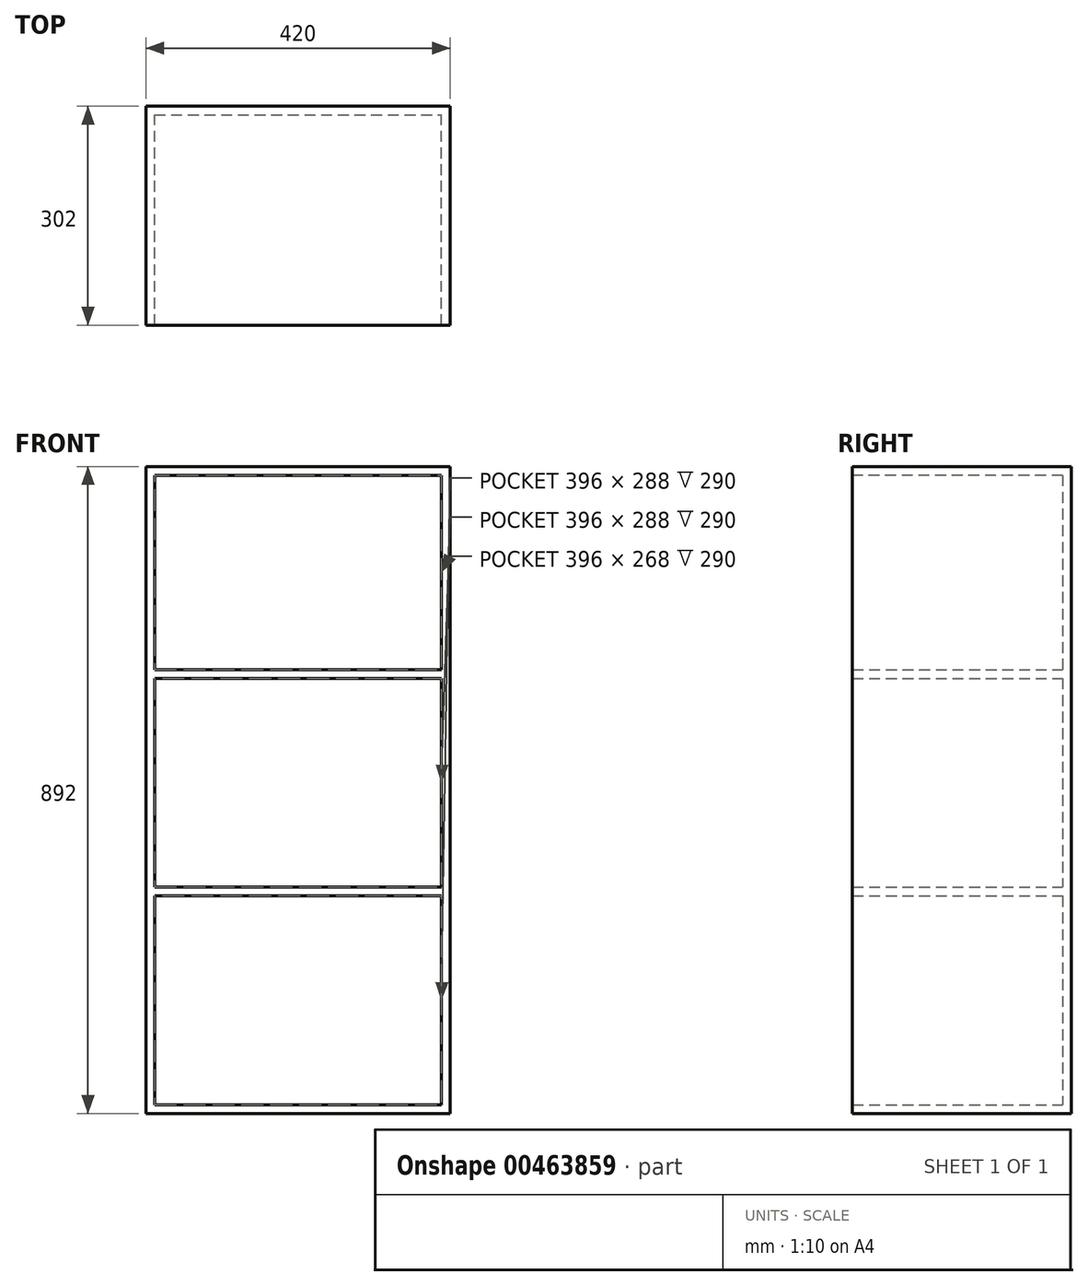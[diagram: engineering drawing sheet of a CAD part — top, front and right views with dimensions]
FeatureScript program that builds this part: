
annotation { "Feature Type Name" : "Feature", "Feature Type Description" : "" }
export const myFeature = defineFeature(function(context is Context, id is Id, definition is map)
    precondition{}
    {
        {
            var Q0;
            Q0=qCreatedBy(makeId("Top.planeOp"),FACE);
            var sketch = newSketch(context, id + "F0", { "sketchPlane" : qUnion([Q0])});
            skLineSegment(sketch, "E0.bottom", {"start": v(0, 0) * mm, "end": v(420, 0) * mm});
            skLineSegment(sketch, "E0.top", {"start": v(0, 290) * mm, "end": v(420, 290) * mm});
            skLineSegment(sketch, "E0.left", {"start": v(0, 0) * mm, "end": v(0, 290) * mm});
            skLineSegment(sketch, "E0.right", {"start": v(420, 0) * mm, "end": v(420, 290) * mm});
            skSolve(sketch);
        }
        {
            var Q0;
            Q0 = qSketchRegion(id + "F0", true);
            extrude(context, id + "F1", {"entities" : qUnion([Q0]), "depth" : 12 * mm});
        }
        {
            var Q0;
            Q0=makeQuery(id+"F1.opExtrude","CAP_FACE",FACE,{"disambiguationData":[OSD([sQuery(id+"F0.wireOp",EDGE,"E0.bottom"),sQuery(id+"F0.wireOp",EDGE,"E0.top"),sQuery(id+"F0.wireOp",EDGE,"E0.left"),sQuery(id+"F0.wireOp",EDGE,"E0.right")])],"isStart":false});
            var sketch = newSketch(context, id + "F2", { "sketchPlane" : qUnion([Q0])});
            skLineSegment(sketch, "E1.bottom", {"start": v(0, 0) * mm, "end": v(12, 0) * mm});
            skLineSegment(sketch, "E1.top", {"start": v(0, 290) * mm, "end": v(12, 290) * mm});
            skLineSegment(sketch, "E1.left", {"start": v(0, 0) * mm, "end": v(0, 290) * mm});
            skLineSegment(sketch, "E1.right", {"start": v(12, 0) * mm, "end": v(12, 290) * mm});
            skLineSegment(sketch, "E2.bottom", {"start": v(420, 0) * mm, "end": v(408, 0) * mm});
            skLineSegment(sketch, "E2.top", {"start": v(420, 290) * mm, "end": v(408, 290) * mm});
            skLineSegment(sketch, "E2.left", {"start": v(420, 0) * mm, "end": v(420, 290) * mm});
            skLineSegment(sketch, "E2.right", {"start": v(408, 0) * mm, "end": v(408, 290) * mm});
            skSolve(sketch);
        }
        {
            var Q0;
            Q0 = qSketchRegion(id + "F2", true);
            extrude(context, id + "F3", {"entities" : qUnion([Q0]), "operationType" : NewBodyOperationType.ADD, "depth" : 880 * mm});
        }
        {
            var Q0;
            Q0=makeQuery(id+"F3.boolean.opBoolean","MERGE",FACE,{"derivedFrom":[makeQuery(id+"F1.opExtrude","SWEPT_FACE",FACE,{"disambiguationData":[OSD([sQuery(id+"F0.wireOp",EDGE,"E0.right")])]}),makeQuery(id+"F3.opExtrude","SWEPT_FACE",FACE,{"disambiguationData":[OSD([sQuery(id+"F2.wireOp",EDGE,"E2.left")])]})]});
            var sketch = newSketch(context, id + "F4", { "sketchPlane" : qUnion([Q0])});
            skPoint(sketch, "E3", {"position": v(0, 300) * mm});
            skPoint(sketch, "E4", {"position": v(0, 600) * mm});
            skLineSegment(sketch, "E5", {"start": v(0, 600) * mm, "end": v(290, 600) * mm});
            skLineSegment(sketch, "E6", {"start": v(0, 300) * mm, "end": v(290, 300) * mm});
            skSolve(sketch);
        }
        {
            var Q0;
            Q0=qCreatedBy(makeId("Top.planeOp"),FACE);
            cPlane(context, id + "F5", {"entities" : qUnion([Q0]), "cplaneType" : CPlaneType.OFFSET, "offset" : 300 * mm, "width" : 152.4 * mm, "height" : 152.4 * mm});
        }
        {
            var Q0;
            Q0=qCreatedBy(makeId("Top.planeOp"),FACE);
            cPlane(context, id + "F6", {"entities" : qUnion([Q0]), "cplaneType" : CPlaneType.OFFSET, "offset" : 600 * mm, "width" : 152.4 * mm, "height" : 152.4 * mm});
        }
        {
            var Q0;
            Q0=qCreatedBy(id+"F5.planeOp",FACE);
            var sketch = newSketch(context, id + "F7", { "sketchPlane" : qUnion([Q0])});
            skLineSegment(sketch, "E7.bottom", {"start": v(0, 0) * mm, "end": v(420, 0) * mm});
            skLineSegment(sketch, "E7.top", {"start": v(0, 290) * mm, "end": v(420, 290) * mm});
            skLineSegment(sketch, "E7.left", {"start": v(0, 0) * mm, "end": v(0, 290) * mm});
            skLineSegment(sketch, "E7.right", {"start": v(420, 0) * mm, "end": v(420, 290) * mm});
            skSolve(sketch);
        }
        {
            var Q0;
            Q0 = qSketchRegion(id + "F7", true);
            extrude(context, id + "F8", {"entities" : qUnion([Q0]), "operationType" : NewBodyOperationType.ADD, "depth" : 12 * mm});
        }
        {
            var Q0;
            Q0=qCreatedBy(id+"F6.planeOp",FACE);
            var sketch = newSketch(context, id + "F9", { "sketchPlane" : qUnion([Q0])});
            skLineSegment(sketch, "E8.bottom", {"start": v(0, 0) * mm, "end": v(420, 0) * mm});
            skLineSegment(sketch, "E8.top", {"start": v(0, 290) * mm, "end": v(420, 290) * mm});
            skLineSegment(sketch, "E8.left", {"start": v(0, 0) * mm, "end": v(0, 290) * mm});
            skLineSegment(sketch, "E8.right", {"start": v(420, 0) * mm, "end": v(420, 290) * mm});
            skSolve(sketch);
        }
        {
            var Q0;
            Q0 = qSketchRegion(id + "F9", true);
            extrude(context, id + "F10", {"entities" : qUnion([Q0]), "operationType" : NewBodyOperationType.ADD, "depth" : 12 * mm});
        }
        {
            var Q0;
            Q0=makeQuery(id+"F3.opExtrude","CAP_EDGE",EDGE,{"disambiguationData":[OSD([sQuery(id+"F2.wireOp",EDGE,"E1.right")])],"isStart":false});
            cPoint(context, id + "F11", {"entities" : qUnion([Q0]), "parameter" : 0.5});
        }
        {
            var Q0;
            Q0=makeQuery(id+"F3.opExtrude","CAP_VERTEX",VERTEX,{"disambiguationData":[OSD([sQuery(id+"F2.wireOp",EDGE,"E1.bottom"),sQuery(id+"F2.wireOp",EDGE,"E1.left")])],"isStart":false});
            var Q1;
            Q1=makeQuery(id+"F3.opExtrude","CAP_VERTEX",VERTEX,{"disambiguationData":[OSD([sQuery(id+"F0.wireOp",EDGE,"E0.bottom"),sQuery(id+"F2.wireOp",EDGE,"E1.bottom"),sQuery(id+"F2.wireOp",EDGE,"E1.right")])],"isStart":false});
            var Q2;
            Q2 = qCreatedBy(id + "F11" ,VERTEX);
            cPlane(context, id + "F12", {"entities" : qUnion([Q0, Q1, Q2]), "cplaneType" : CPlaneType.THREE_POINT, "offset" : 25.4 * mm, "width" : 152.4 * mm, "height" : 152.4 * mm});
        }
        {
            var Q0;
            Q0=qCreatedBy(id+"F12.planeOp",FACE);
            var sketch = newSketch(context, id + "F13", { "sketchPlane" : qUnion([Q0])});
            skLineSegment(sketch, "E9.bottom", {"start": v(0, 0) * mm, "end": v(420, 0) * mm});
            skLineSegment(sketch, "E9.top", {"start": v(0, -290) * mm, "end": v(420, -290) * mm});
            skLineSegment(sketch, "E9.left", {"start": v(0, 0) * mm, "end": v(0, -290) * mm});
            skLineSegment(sketch, "E9.right", {"start": v(420, 0) * mm, "end": v(420, -290) * mm});
            skSolve(sketch);
        }
        {
            var Q0;
            Q0 = qSketchRegion(id + "F13", true);
            extrude(context, id + "F14", {"entities" : qUnion([Q0]), "operationType" : NewBodyOperationType.ADD, "depth" : 12 * mm});
        }
        {
            var Q0;
            Q0=makeQuery(id+"F14.boolean.opBoolean","MERGE",FACE,{"derivedFrom":[makeQuery(id+"F10.boolean.opBoolean","MERGE",FACE,{"derivedFrom":[makeQuery(id+"F8.boolean.opBoolean","MERGE",FACE,{"derivedFrom":[makeQuery(id+"F3.boolean.opBoolean","MERGE",FACE,{"derivedFrom":[makeQuery(id+"F1.opExtrude","SWEPT_FACE",FACE,{"disambiguationData":[OSD([sQuery(id+"F0.wireOp",EDGE,"E0.top")])]}),makeQuery(id+"F3.opExtrude","SWEPT_FACE",FACE,{"disambiguationData":[OSD([sQuery(id+"F2.wireOp",EDGE,"E1.top")])]}),makeQuery(id+"F3.opExtrude","SWEPT_FACE",FACE,{"disambiguationData":[OSD([sQuery(id+"F2.wireOp",EDGE,"E2.top")])]})]}),makeQuery(id+"F8.opExtrude","SWEPT_FACE",FACE,{"disambiguationData":[OSD([sQuery(id+"F7.wireOp",EDGE,"E7.top")])]})]}),makeQuery(id+"F10.opExtrude","SWEPT_FACE",FACE,{"disambiguationData":[OSD([sQuery(id+"F9.wireOp",EDGE,"E8.top")])]})]}),makeQuery(id+"F14.opExtrude","SWEPT_FACE",FACE,{"disambiguationData":[OSD([sQuery(id+"F13.wireOp",EDGE,"E9.top")])]})]});
            var sketch = newSketch(context, id + "F15", { "sketchPlane" : qUnion([Q0])});
            skLineSegment(sketch, "E10.bottom", {"start": v(0, 0) * mm, "end": v(-420, 0) * mm});
            skLineSegment(sketch, "E10.top", {"start": v(0, 892) * mm, "end": v(-420, 892) * mm});
            skLineSegment(sketch, "E10.left", {"start": v(0, 0) * mm, "end": v(0, 892) * mm});
            skLineSegment(sketch, "E10.right", {"start": v(-420, 0) * mm, "end": v(-420, 892) * mm});
            skSolve(sketch);
        }
        {
            var Q0;
            Q0 = qSketchRegion(id + "F15", true);
            extrude(context, id + "F16", {"entities" : qUnion([Q0]), "operationType" : NewBodyOperationType.ADD, "depth" : 12 * mm});
        }
    });
